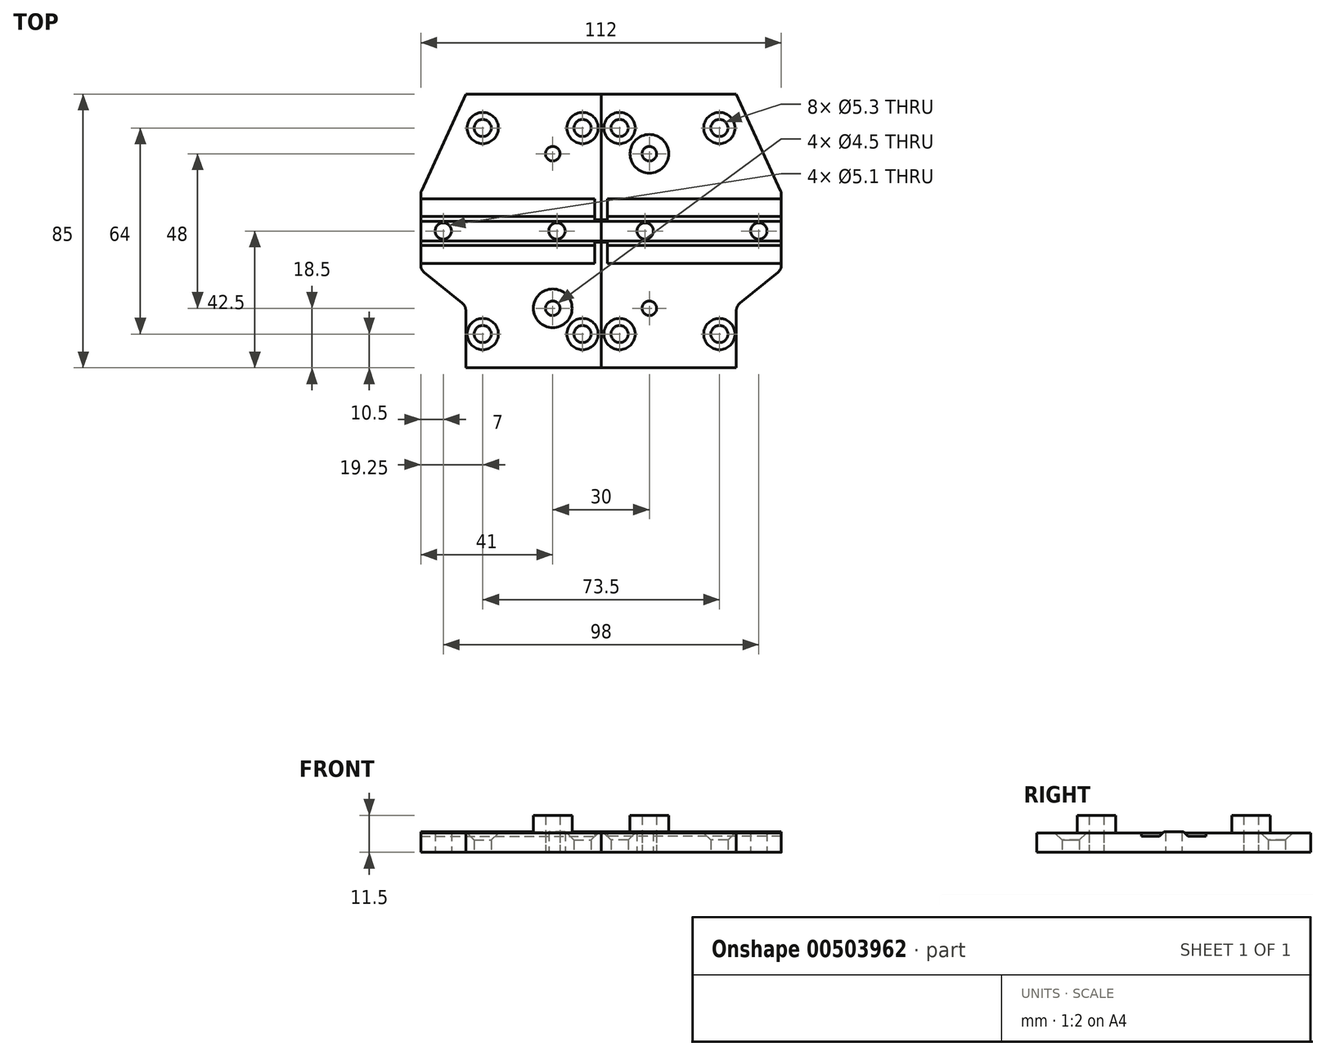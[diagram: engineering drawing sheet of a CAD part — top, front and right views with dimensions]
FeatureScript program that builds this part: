
annotation { "Feature Type Name" : "Feature", "Feature Type Description" : "" }
export const myFeature = defineFeature(function(context is Context, id is Id, definition is map)
    precondition{}
    {
        {
            var Q0;
            Q0=qCreatedBy(makeId("Top.planeOp"),FACE);
            var sketch = newSketch(context, id + "F0", { "sketchPlane" : qUnion([Q0])});
            skLineSegment(sketch, "E0", {"start": v(0, 85) * mm, "end": v(0, 0) * mm});
            skLineSegment(sketch, "E1", {"start": v(56, 30.5) * mm, "end": v(56, 54.5) * mm});
            skCircle(sketch, "E2", {"center": v(5.75, 10.5) * mm, "radius": 2.65 * mm});
            skCircle(sketch, "E3", {"center": v(36.75, 10.5) * mm, "radius": 2.65 * mm});
            skCircle(sketch, "E4", {"center": v(5.75, 74.5) * mm, "radius": 2.65 * mm});
            skCircle(sketch, "E5", {"center": v(36.75, 74.5) * mm, "radius": 2.65 * mm});
            skLineSegment(sketch, "E6", {"start": v(0, 42.5) * mm, "end": v(56, 42.5) * mm, "construction": true});
            skCircle(sketch, "E7", {"center": v(13.7, 42.5) * mm, "radius": 2.55 * mm});
            skCircle(sketch, "E8", {"center": v(49, 42.5) * mm, "radius": 2.55 * mm});
            skLineSegment(sketch, "E9", {"start": v(15, 85) * mm, "end": v(15, 0) * mm, "construction": true});
            skCircle(sketch, "E10", {"center": v(15, 66.5) * mm, "radius": 2.25 * mm});
            skCircle(sketch, "E11", {"center": v(15, 18.5) * mm, "radius": 2.25 * mm});
            skLineSegment(sketch, "E12", {"start": v(56, 54.5) * mm, "end": v(42, 85) * mm});
            skLineSegment(sketch, "E13", {"start": v(56, 30.5) * mm, "end": v(42, 19.19) * mm});
            skLineSegment(sketch, "E14", {"start": v(42, 19.19) * mm, "end": v(42, 0) * mm});
            skLineSegment(sketch, "E15", {"start": v(0, 0) * mm, "end": v(42, 0) * mm});
            skLineSegment(sketch, "E16", {"start": v(0, 85) * mm, "end": v(42, 85) * mm});
            skLineSegment(sketch, "E17", {"start": v(5.75, 10.5) * mm, "end": v(36.75, 10.5) * mm, "construction": true});
            skLineSegment(sketch, "E18", {"start": v(21.25, 10.5) * mm, "end": v(21.25, 85) * mm, "construction": true});
            skSolve(sketch);
        }
        {
            var Q0;
            Q0=makeQuery(id+"F0.imprint","IMPRINT",FACE,{"disambiguationData":[TD([[makeQuery(id+"F0.imprint","IMPRINT",EDGE,{"derivedFrom":sQuery(id+"F0.wireOp",EDGE,"E0")}),1.0]])]});
            extrude(context, id + "F1", {"entities" : qUnion([Q0]), "depth" : 6 * mm, "offsetDistance" : 25 * mm});
        }
        {
            var Q0;
            Q0=makeQuery(id+"F1.opExtrude","CAP_EDGE",EDGE,{"disambiguationData":[OSD([sQuery(id+"F0.wireOp",EDGE,"7PE5ZSEU-JcNk-cLVh-wpRH-j7cBejXt5jF8")])],"isStart":false});
            var Q1;
            Q1=makeQuery(id+"F1.opExtrude","CAP_EDGE",EDGE,{"disambiguationData":[OSD([sQuery(id+"F0.wireOp",EDGE,"E2")])],"isStart":false});
            var Q2;
            Q2=makeQuery(id+"F1.opExtrude","CAP_EDGE",EDGE,{"disambiguationData":[OSD([sQuery(id+"F0.wireOp",EDGE,"E3")])],"isStart":false});
            var Q3;
            Q3=makeQuery(id+"F1.opExtrude","CAP_EDGE",EDGE,{"disambiguationData":[OSD([sQuery(id+"F0.wireOp",EDGE,"EACFaYuQ-H4Gb-WAH1-6icg-fq9vRwD7qrK0")])],"isStart":false});
            var Q4;
            Q4=makeQuery(id+"F1.opExtrude","CAP_EDGE",EDGE,{"disambiguationData":[OSD([sQuery(id+"F0.wireOp",EDGE,"zTDOp5FC-UEsi-jjVO-lvdK-QSJ0sNU9pkqq")])],"isStart":false});
            var Q5;
            Q5=makeQuery(id+"F1.opExtrude","CAP_EDGE",EDGE,{"disambiguationData":[OSD([sQuery(id+"F0.wireOp",EDGE,"IUMH0RMi-mbiA-5vrg-e3gO-govUD7INfHBy")])],"isStart":false});
            var Q6;
            Q6=makeQuery(id+"F1.opExtrude","CAP_EDGE",EDGE,{"disambiguationData":[OSD([sQuery(id+"F0.wireOp",EDGE,"E4")])],"isStart":false});
            var Q7;
            Q7=makeQuery(id+"F1.opExtrude","CAP_EDGE",EDGE,{"disambiguationData":[OSD([sQuery(id+"F0.wireOp",EDGE,"E5")])],"isStart":false});
            chamfer(context, id + "F2", {"entities" : qUnion([Q0, Q1, Q2, Q3, Q4, Q5, Q6, Q7]), "width" : 2.2 * mm, "tangentPropagation" : true});
        }
        {
            var Q0;
            Q0=makeQuery(id+"F1.opExtrude","SWEPT_FACE",FACE,{"disambiguationData":[OSD([sQuery(id+"F0.wireOp",EDGE,"E0")])]});
            var sketch = newSketch(context, id + "F3", { "sketchPlane" : qUnion([Q0])});
            skLineSegment(sketch, "E19", {"start": v(-42.5, 6) * mm, "end": v(-42.5, 0) * mm, "construction": true});
            skLineSegment(sketch, "E20.bottom", {"start": v(-52.55, 6) * mm, "end": v(-32.45, 6) * mm, "construction": true});
            skLineSegment(sketch, "E20.top", {"start": v(-52.55, 5) * mm, "end": v(-32.45, 5) * mm, "construction": true});
            skLineSegment(sketch, "E20.left", {"start": v(-52.55, 6) * mm, "end": v(-52.55, 5) * mm, "construction": true});
            skLineSegment(sketch, "E20.right", {"start": v(-32.45, 6) * mm, "end": v(-32.45, 5) * mm, "construction": true});
            skLineSegment(sketch, "E21", {"start": v(-47, 5) * mm, "end": v(-45.55, 6.46) * mm});
            skLineSegment(sketch, "E22", {"start": v(-45.55, 6.46) * mm, "end": v(-39.45, 6.46) * mm});
            skLineSegment(sketch, "E23", {"start": v(-39.45, 6.46) * mm, "end": v(-38, 5) * mm});
            skLineSegment(sketch, "E24", {"start": v(-52.55, 6) * mm, "end": v(-52.55, 5) * mm});
            skLineSegment(sketch, "E25", {"start": v(-52.55, 5) * mm, "end": v(-47, 5) * mm});
            skLineSegment(sketch, "E26", {"start": v(-38, 5) * mm, "end": v(-32.45, 5) * mm});
            skLineSegment(sketch, "E27", {"start": v(-32.45, 5) * mm, "end": v(-32.45, 6) * mm});
            skSolve(sketch);
        }
        {
            var Q0;
            {var subQ4=sQuery(id+"F3.wireOp",EDGE,"E24");Q0=makeQuery(id+"F3.imprint","IMPRINT",FACE,{"disambiguationData":[TD([[makeQuery(id+"F3.imprint","IMPRINT",EDGE,{"derivedFrom":subQ4}),1.0]])]});}
            var Q1;
            {var subQ0=sQuery(id+"F3.wireOp",EDGE,"E26");Q1=makeQuery(id+"F3.imprint","IMPRINT",FACE,{"disambiguationData":[TD([[makeQuery(id+"F3.imprint","IMPRINT",EDGE,{"derivedFrom":subQ0}),1.0]])]});}
            extrude(context, id + "F4", {"entities" : qUnion([Q0, Q1]), "operationType" : NewBodyOperationType.REMOVE, "endBound" : BoundingType.THROUGH_ALL, "oppositeDirection" : true, "depth" : 25 * mm, "offsetDistance" : 25 * mm, "hasSecondDirection" : true, "secondDirectionOppositeDirection" : true, "secondDirectionDepth" : 2 * mm});
        }
        {
            var Q0;
            {var subQ0=sQuery(id+"F3.wireOp",EDGE,"E22");Q0=makeQuery(id+"F3.imprint","IMPRINT",FACE,{"disambiguationData":[TD([[makeQuery(id+"F3.imprint","IMPRINT",EDGE,{"derivedFrom":subQ0}),-1.0]])]});}
            var Q1;
            Q1=makeQuery(id+"F1.opExtrude","SWEPT_FACE",FACE,{"disambiguationData":[OSD([sQuery(id+"F0.wireOp",EDGE,"E1")])]});
            extrude(context, id + "F5", {"entities" : qUnion([Q0]), "operationType" : NewBodyOperationType.ADD, "endBound" : BoundingType.UP_TO_SURFACE, "oppositeDirection" : true, "depth" : 25 * mm, "endBoundEntityFace" : qUnion([Q1]), "offsetDistance" : 25 * mm});
        }
        {
            var Q0;
            Q0=makeQuery(id+"F5.boolean.opBoolean","SPLIT",FACE,{"disambiguationData":[TD([makeQuery(id+"F1.opExtrude","SWEPT_FACE",FACE,{"disambiguationData":[OSD([sQuery(id+"F0.wireOp",EDGE,"E7")])]})])],"derivedFrom":makeQuery(id+"F5.opExtrude","SWEPT_FACE",FACE,{"disambiguationData":[OSD([sQuery(id+"F0.wireOp",EDGE,"E0")])]})});
            var Q1;
            Q1=makeQuery(id+"F5.boolean.opBoolean","SPLIT",FACE,{"disambiguationData":[TD([makeQuery(id+"F1.opExtrude","SWEPT_FACE",FACE,{"disambiguationData":[OSD([sQuery(id+"F0.wireOp",EDGE,"E8")])]})])],"derivedFrom":makeQuery(id+"F5.opExtrude","SWEPT_FACE",FACE,{"disambiguationData":[OSD([sQuery(id+"F0.wireOp",EDGE,"E0")])]})});
            extrude(context, id + "F6", {"entities" : qUnion([Q0, Q1]), "operationType" : NewBodyOperationType.REMOVE, "oppositeDirection" : true, "depth" : 25 * mm, "offsetDistance" : 25 * mm});
        }
        {
            var Q0;
            Q0=makeQuery(id+"F1.opExtrude","SWEPT_EDGE",EDGE,{"disambiguationData":[OSD([sQuery(id+"F0.wireOp",EDGE,"E13"),sQuery(id+"F0.wireOp",EDGE,"E14")])]});
            var Q1;
            Q1=makeQuery(id+"F1.opExtrude","SWEPT_EDGE",EDGE,{"disambiguationData":[OSD([sQuery(id+"F0.wireOp",EDGE,"E1"),sQuery(id+"F0.wireOp",EDGE,"E13")])]});
            var Q2;
            Q2=makeQuery(id+"F1.opExtrude","SWEPT_EDGE",EDGE,{"disambiguationData":[OSD([sQuery(id+"F0.wireOp",EDGE,"E1"),sQuery(id+"F0.wireOp",EDGE,"E12")])]});
            fillet(context, id + "F7", {"entities" : qUnion([Q0, Q1, Q2]), "radius" : 3 * mm, "tangentPropagation" : true, "allowEdgeOverflow" : false});
        }
        {
            var Q0;
            {var subQ1=sQuery(id+"F0.wireOp",EDGE,"E1");var subQ3=sQuery(id+"F0.wireOp",EDGE,"E5");var subQ4=sQuery(id+"F0.wireOp",EDGE,"E12");var subQ5=sQuery(id+"F0.wireOp",EDGE,"E4");var subQ6=sQuery(id+"F0.wireOp",EDGE,"E16");var subQ7=sQuery(id+"F0.wireOp",EDGE,"E0");var subQ8=sQuery(id+"F0.wireOp",EDGE,"E10");Q0=makeQuery(id+"F5.boolean.opBoolean","SPLIT",FACE,{"disambiguationData":[TD([makeQuery(id+"F1.opExtrude","SWEPT_FACE",FACE,{"disambiguationData":[OSD([subQ8])]})])],"derivedFrom":makeQuery(id+"F1.opExtrude","CAP_FACE",FACE,{"disambiguationData":[OSD([subQ7,subQ1,sQuery(id+"F0.wireOp",EDGE,"E2"),sQuery(id+"F0.wireOp",EDGE,"E3"),subQ5,subQ3,sQuery(id+"F0.wireOp",EDGE,"E7"),sQuery(id+"F0.wireOp",EDGE,"E8"),subQ8,sQuery(id+"F0.wireOp",EDGE,"E11"),subQ4,sQuery(id+"F0.wireOp",EDGE,"E13"),sQuery(id+"F0.wireOp",EDGE,"E14"),sQuery(id+"F0.wireOp",EDGE,"E15"),subQ6])],"isStart":false})});}
            cPlane(context, id + "F8", {"entities" : qUnion([Q0]), "cplaneType" : CPlaneType.OFFSET, "offset" : 0 * mm, "width" : 150 * mm, "height" : 150 * mm});
        }
        {
            var Q0;
            Q0=makeQuery(id+"F1.opExtrude","SWEPT_BODY",BODY,{"disambiguationData":[OSD([sQuery(id+"F0.wireOp",EDGE,"E0"),sQuery(id+"F0.wireOp",EDGE,"E1"),sQuery(id+"F0.wireOp",EDGE,"E2"),sQuery(id+"F0.wireOp",EDGE,"E3"),sQuery(id+"F0.wireOp",EDGE,"E4"),sQuery(id+"F0.wireOp",EDGE,"E5"),sQuery(id+"F0.wireOp",EDGE,"E7"),sQuery(id+"F0.wireOp",EDGE,"E8"),sQuery(id+"F0.wireOp",EDGE,"E10"),sQuery(id+"F0.wireOp",EDGE,"E11"),sQuery(id+"F0.wireOp",EDGE,"E12"),sQuery(id+"F0.wireOp",EDGE,"E13"),sQuery(id+"F0.wireOp",EDGE,"E14"),sQuery(id+"F0.wireOp",EDGE,"E15"),sQuery(id+"F0.wireOp",EDGE,"E16")])]});
            var Q1;
            {var subQ3=sQuery(id+"F3.wireOp",EDGE,"E24");Q1=makeQuery(id+"F3.imprint","IMPRINT",FACE,{"disambiguationData":[TD([[makeQuery(id+"F3.imprint","IMPRINT",EDGE,{"derivedFrom":subQ3}),-1.0]])]});}
            mirror(context, id + "F9", {"entities" : qUnion([Q0]), "mirrorPlane" : qUnion([Q1])});
        }
        {
            var Q0;
            Q0=qCreatedBy(id+"F8.planeOp",FACE);
            var sketch = newSketch(context, id + "F10", { "sketchPlane" : qUnion([Q0])});
            skCircle(sketch, "E28", {"center": v(15, 66.5) * mm, "radius": 6 * mm});
            skCircle(sketch, "E29", {"center": v(-15, 18.5) * mm, "radius": 6 * mm});
            skCircle(sketch, "E30.0", {"center": v(15, 66.5) * mm, "radius": 2.25 * mm});
            skCircle(sketch, "E31.0", {"center": v(-15, 18.5) * mm, "radius": 2.25 * mm});
            skSolve(sketch);
        }
        {
            var Q0;
            Q0=makeQuery(id+"F10.imprint","IMPRINT",FACE,{"disambiguationData":[TD([[makeQuery(id+"F10.imprint","IMPRINT",EDGE,{"derivedFrom":sQuery(id+"F10.wireOp",EDGE,"E28")}),1.0]])]});
            var Q1;
            Q1=makeQuery(id+"F10.imprint","IMPRINT",FACE,{"disambiguationData":[TD([[makeQuery(id+"F10.imprint","IMPRINT",EDGE,{"derivedFrom":sQuery(id+"F10.wireOp",EDGE,"E29")}),1.0]])]});
            extrude(context, id + "F11", {"entities" : qUnion([Q0, Q1]), "operationType" : NewBodyOperationType.ADD, "depth" : 5.5 * mm, "offsetDistance" : 25 * mm});
        }
    });
